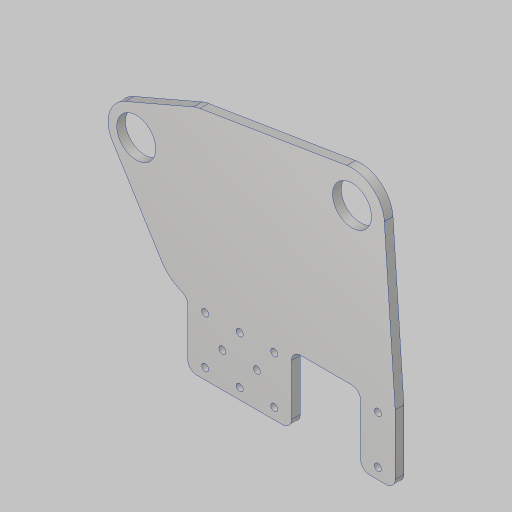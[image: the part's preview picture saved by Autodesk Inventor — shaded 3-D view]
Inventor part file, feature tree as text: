
AUTODESK INVENTOR PART (.ipt)
format: ipt  version: 2023.5 (Build 275446000, 446)  size: 252,928 bytes
history: native  units: in
note: dims shown in document units (in); Inventor stores cm internally (conversion verified against a paired STEP export)
features: sketch x3, extrude x3, fillet x2, hole x1, projected_geometry x1
ambient origin geometry x8: Origin, YZ Plane, XZ Plane, XY Plane, X Axis, Y Axis, Z Axis, Center Point
bodies: Solid1 (feature_tree)
feature tree (10):
  sketch  "Sketch1"  dims[d0=6.0in d1=2.0in]
  sketch  "Sketch2"  dims[d2=1.375in d3=0.5in d4=1.25in]
  extrude  "Extrusion1"  Depth=2.0in
  hole  "Hole1"  [1 undecoded]
  fillet  "Fillet1"  Radius=1.25in
  sketch  "Sketch4"  dims[d5=1.25in d6=1.375in d7=1.0in d8=0.375in d9=0.5in d10=0.5in d11=0.5in d12=0.5in d13=0.5in d14=4.38in d15=5.0in d16=3.0in d17=1.125in d18=0.375in d20=0.375in d21=0.375in d22=0.25in d23=0.0in d24=0.201in d25=0.75in d26=0.375in d27=0.25in d28=0.5635in d29=1.0in d30=0.8108in d31=6.5in d32=0.75in d33=0.26in d45=2.0in d46=2.4in d47=0.75in d48=0.5in d49=3.6in d50=0.25in d52=8.0in d53=2.0in d54=3.0in d55=1.125in d56=0.25in d57=1.0in d58=3.3in d59=2.275in d60=1.0in d61=3.3in d62=2.9288in d64=0.25in d65=0.25in d66=1.0in d67=0.0in d68=2.3622in d70=360.0deg d72=0.0in d73=0.0in d82=3.342in d83=0.58in d85=0.26in d86=1.114in d92=6.3055in d93=5.834in d94=1.5551in]
  extrude  "Extrusion3"  Depth=0.26in
  extrude  "Extrusion4"  Depth=1.0in
  fillet  "Fillet4"  Radius=0.375in
  projected_geometry  "Project Cut Edges2"
note: 1 required parameter value undecoded (feature->parameter linkage not recoverable at this tier; creation-order binding heuristic only, values carry confidence <= 0.55)
